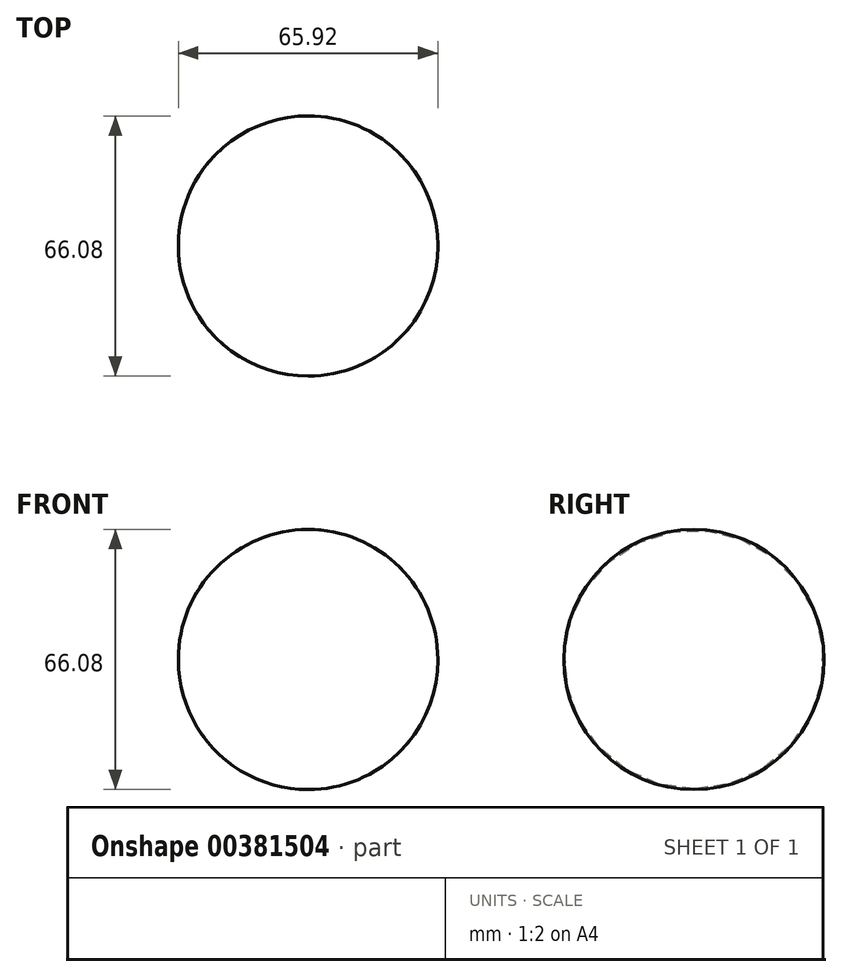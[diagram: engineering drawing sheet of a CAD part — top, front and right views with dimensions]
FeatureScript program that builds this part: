
annotation { "Feature Type Name" : "Feature", "Feature Type Description" : "" }
export const myFeature = defineFeature(function(context is Context, id is Id, definition is map)
    precondition{}
    {
        {
            var Q0;
            Q0=qCreatedBy(makeId("Front.planeOp"),FACE);
            var sketch = newSketch(context, id + "F0", { "sketchPlane" : qUnion([Q0])});
            skArc(sketch, "E0", {"start": v(32.96, 0.08) * mm, "mid": v(0, 32.96) * mm, "end": v(-32.96, 0.08) * mm});
            skLineSegment(sketch, "E1", {"start": v(-32.96, 0.08) * mm, "end": v(32.96, 0.08) * mm});
            skSolve(sketch);
        }
        {
            var Q0;
            Q0=makeQuery(id+"F0.imprint","IMPRINT",FACE,{"disambiguationData":[TD([[makeQuery(id+"F0.imprint","IMPRINT",EDGE,{"derivedFrom":sQuery(id+"F0.wireOp",EDGE,"E0")}),1.0]])]});
            var Q1;
            Q1=sQuery(id+"F0.wireOp",EDGE,"E1");
            revolve(context, id + "F1", {"entities" : qUnion([Q0]), "axis" : qUnion([Q1]), "revolveType" : RevolveType.FULL});
        }
    });
